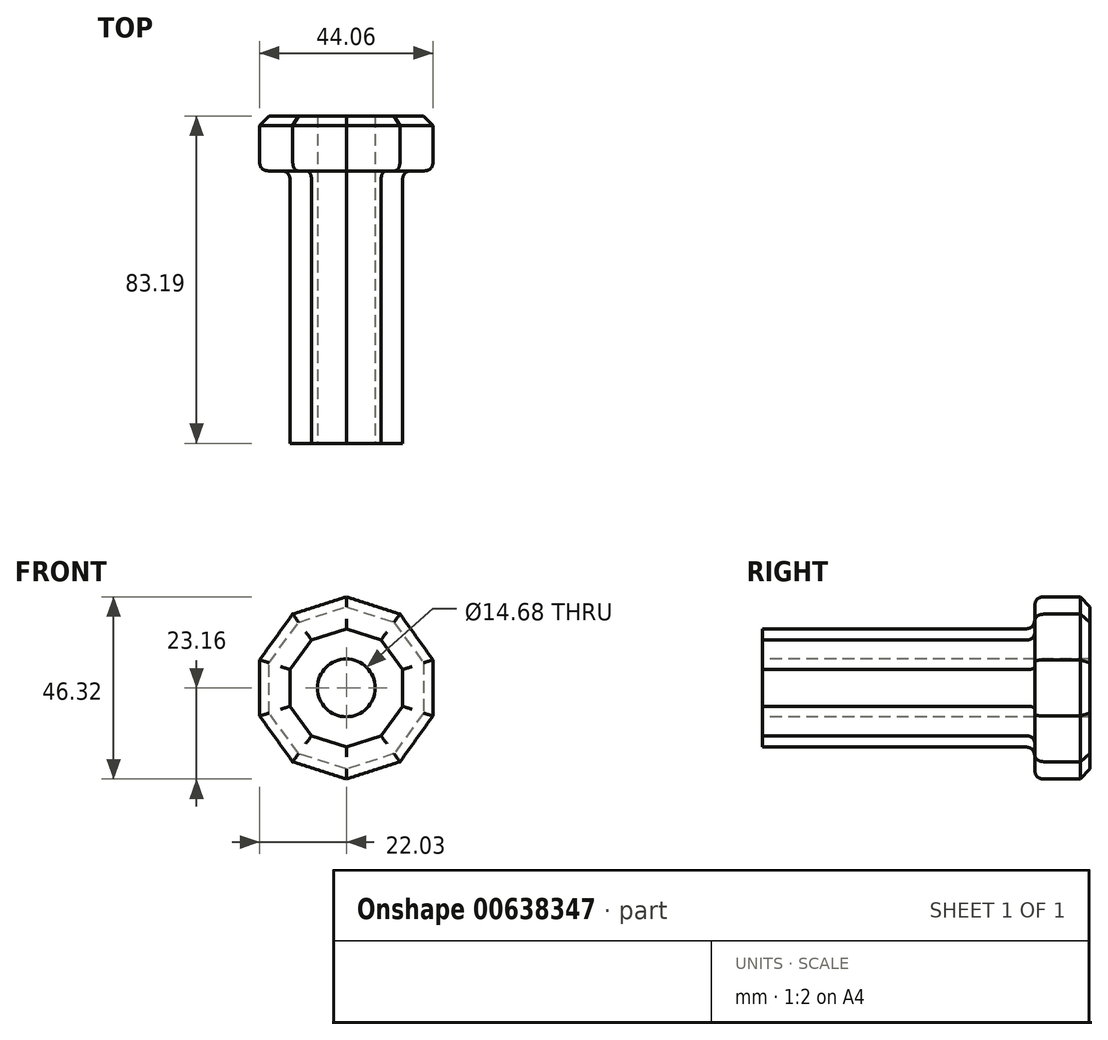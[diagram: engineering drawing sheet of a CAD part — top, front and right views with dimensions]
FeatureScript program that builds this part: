
annotation { "Feature Type Name" : "Feature", "Feature Type Description" : "" }
export const myFeature = defineFeature(function(context is Context, id is Id, definition is map)
    precondition{}
    {
        {
            var Q0;
            Q0=qCreatedBy(makeId("Front.planeOp"),FACE);
            var sketch = newSketch(context, id + "F0", { "sketchPlane" : qUnion([Q0])});
            skCircle(sketch, "E0.cCircle", {"center": v(0, 0) * mm, "radius": 14.29 * mm, "construction": true});
            skLineSegment(sketch, "E0.0", {"start": v(-14.29, -4.64) * mm, "end": v(-14.29, 4.64) * mm});
            skLineSegment(sketch, "E0.1", {"start": v(-14.29, 4.64) * mm, "end": v(-8.83, 12.15) * mm});
            skLineSegment(sketch, "E0.2", {"start": v(-8.83, 12.15) * mm, "end": v(0, 15.02) * mm});
            skLineSegment(sketch, "E0.3", {"start": v(0, 15.02) * mm, "end": v(8.83, 12.15) * mm});
            skLineSegment(sketch, "E0.4", {"start": v(8.83, 12.15) * mm, "end": v(14.29, 4.64) * mm});
            skLineSegment(sketch, "E0.5", {"start": v(14.29, 4.64) * mm, "end": v(14.29, -4.64) * mm});
            skLineSegment(sketch, "E0.6", {"start": v(14.29, -4.64) * mm, "end": v(8.83, -12.15) * mm});
            skLineSegment(sketch, "E0.7", {"start": v(8.83, -12.15) * mm, "end": v(0, -15.02) * mm});
            skLineSegment(sketch, "E0.8", {"start": v(0, -15.02) * mm, "end": v(-8.83, -12.15) * mm});
            skLineSegment(sketch, "E0.9", {"start": v(-8.83, -12.15) * mm, "end": v(-14.29, -4.64) * mm});
            skPoint(sketch, "E0.0.midPoint", {"position": v(-14.29, 0) * mm});
            skSolve(sketch);
        }
        {
            var Q0;
            Q0 = qSketchRegion(id + "F0", true);
            extrude(context, id + "F1", {"entities" : qUnion([Q0]), "depth" : 76.2 * mm, "offsetDistance" : 25.4 * mm});
        }
        {
            var Q0;
            Q0=qCreatedBy(makeId("Front.planeOp"),FACE);
            var sketch = newSketch(context, id + "F2", { "sketchPlane" : qUnion([Q0])});
            skCircle(sketch, "E1.cCircle", {"center": v(0, 0) * mm, "radius": 22.03 * mm, "construction": true});
            skLineSegment(sketch, "E1.0", {"start": v(-22.03, -7.16) * mm, "end": v(-22.03, 7.16) * mm});
            skLineSegment(sketch, "E1.1", {"start": v(-22.03, 7.16) * mm, "end": v(-13.62, 18.74) * mm});
            skLineSegment(sketch, "E1.2", {"start": v(-13.62, 18.74) * mm, "end": v(0, 23.16) * mm});
            skLineSegment(sketch, "E1.3", {"start": v(0, 23.16) * mm, "end": v(13.62, 18.74) * mm});
            skLineSegment(sketch, "E1.4", {"start": v(13.62, 18.74) * mm, "end": v(22.03, 7.16) * mm});
            skLineSegment(sketch, "E1.5", {"start": v(22.03, 7.16) * mm, "end": v(22.03, -7.16) * mm});
            skLineSegment(sketch, "E1.6", {"start": v(22.03, -7.16) * mm, "end": v(13.62, -18.74) * mm});
            skLineSegment(sketch, "E1.7", {"start": v(13.62, -18.74) * mm, "end": v(0, -23.16) * mm});
            skLineSegment(sketch, "E1.8", {"start": v(0, -23.16) * mm, "end": v(-13.62, -18.74) * mm});
            skLineSegment(sketch, "E1.9", {"start": v(-13.62, -18.74) * mm, "end": v(-22.03, -7.16) * mm});
            skPoint(sketch, "E1.0.midPoint", {"position": v(-22.03, 0) * mm});
            skSolve(sketch);
        }
        {
            var Q0;
            Q0=makeQuery(id+"F2.imprint","IMPRINT",FACE,{"disambiguationData":[TD([[makeQuery(id+"F2.imprint","IMPRINT",EDGE,{"derivedFrom":sQuery(id+"F2.wireOp",EDGE,"E1.0")}),-1.0]])]});
            extrude(context, id + "F3", {"entities" : qUnion([Q0]), "operationType" : NewBodyOperationType.ADD, "endBound" : BoundingType.SYMMETRIC, "depth" : 13.97 * mm, "offsetDistance" : 25.4 * mm});
        }
        {
            var Q0;
            Q0=makeQuery(id+"F3.opExtrude","CAP_FACE",FACE,{"disambiguationData":[OSD([sQuery(id+"F2.wireOp",EDGE,"E1.0"),sQuery(id+"F2.wireOp",EDGE,"E1.1"),sQuery(id+"F2.wireOp",EDGE,"E1.2"),sQuery(id+"F2.wireOp",EDGE,"E1.3"),sQuery(id+"F2.wireOp",EDGE,"E1.4"),sQuery(id+"F2.wireOp",EDGE,"E1.5"),sQuery(id+"F2.wireOp",EDGE,"E1.6"),sQuery(id+"F2.wireOp",EDGE,"E1.7"),sQuery(id+"F2.wireOp",EDGE,"E1.8"),sQuery(id+"F2.wireOp",EDGE,"E1.9")])],"isStart":false});
            fillet(context, id + "F4", {"entities" : qUnion([Q0]), "radius" : 2.41 * mm, "tangentPropagation" : true, "rho" : 0.5, "crossSection" : FilletCrossSection.CONIC, "allowEdgeOverflow" : false});
        }
        {
            var Q0;
            Q0=makeQuery(id+"F3.opExtrude","CAP_FACE",FACE,{"disambiguationData":[OSD([sQuery(id+"F2.wireOp",EDGE,"E1.0"),sQuery(id+"F2.wireOp",EDGE,"E1.1"),sQuery(id+"F2.wireOp",EDGE,"E1.2"),sQuery(id+"F2.wireOp",EDGE,"E1.3"),sQuery(id+"F2.wireOp",EDGE,"E1.4"),sQuery(id+"F2.wireOp",EDGE,"E1.5"),sQuery(id+"F2.wireOp",EDGE,"E1.6"),sQuery(id+"F2.wireOp",EDGE,"E1.7"),sQuery(id+"F2.wireOp",EDGE,"E1.8"),sQuery(id+"F2.wireOp",EDGE,"E1.9")])],"isStart":true});
            chamfer(context, id + "F5", {"entities" : qUnion([Q0]), "width" : 2.41 * mm, "tangentPropagation" : true});
        }
        {
            var Q0;
            Q0=makeQuery(id+"F1.opExtrude","CAP_FACE",FACE,{"disambiguationData":[OSD([sQuery(id+"F0.wireOp",EDGE,"E0.0"),sQuery(id+"F0.wireOp",EDGE,"E0.1"),sQuery(id+"F0.wireOp",EDGE,"E0.2"),sQuery(id+"F0.wireOp",EDGE,"E0.3"),sQuery(id+"F0.wireOp",EDGE,"E0.4"),sQuery(id+"F0.wireOp",EDGE,"E0.5"),sQuery(id+"F0.wireOp",EDGE,"E0.6"),sQuery(id+"F0.wireOp",EDGE,"E0.7"),sQuery(id+"F0.wireOp",EDGE,"E0.8"),sQuery(id+"F0.wireOp",EDGE,"E0.9")])],"isStart":false});
            var sketch = newSketch(context, id + "F6", { "sketchPlane" : qUnion([Q0])});
            skCircle(sketch, "E2", {"center": v(0, 0) * mm, "radius": 9.46 * mm});
            skSolve(sketch);
        }
        {
            var Q0;
            Q0=sQuery(id+"F6.wireOp",VERTEX,"E2.center");
            var Q1;
            Q1=makeQuery(id+"F1.opExtrude","SWEPT_BODY",BODY,{"disambiguationData":[OSD([sQuery(id+"F0.wireOp",EDGE,"E0.0"),sQuery(id+"F0.wireOp",EDGE,"E0.1"),sQuery(id+"F0.wireOp",EDGE,"E0.2"),sQuery(id+"F0.wireOp",EDGE,"E0.3"),sQuery(id+"F0.wireOp",EDGE,"E0.4"),sQuery(id+"F0.wireOp",EDGE,"E0.5"),sQuery(id+"F0.wireOp",EDGE,"E0.6"),sQuery(id+"F0.wireOp",EDGE,"E0.7"),sQuery(id+"F0.wireOp",EDGE,"E0.8"),sQuery(id+"F0.wireOp",EDGE,"E0.9")])]});
            hole(context, id + "F7", {"style" : HoleStyle.SIMPLE, "endStyle" : HoleEndStyle.THROUGH, "standardTappedOrClearance" : lookupTablePath({ "standard" : "ANSI", "engagement" : "75%", "pitch" : "18 tpi", "size" : "5/8", "type" : "Tapped" }), "standardBlindInLast" : lookupTablePath({ "standard" : "ANSI", "engagement" : "75%", "pitch" : "18 tpi", "size" : "5/8", "type" : "Tapped" }), "holeDiameter" : 14.68 * mm, "majorDiameter" : 15.88 * mm, "showTappedDepth" : true, "isTappedThrough" : true, "tappedDepth" : 12.7 * mm, "tapClearance" : 3, "startFromSketch" : true, "locations" : qUnion([Q0]), "scope" : qUnion([Q1])});
        }
    });
